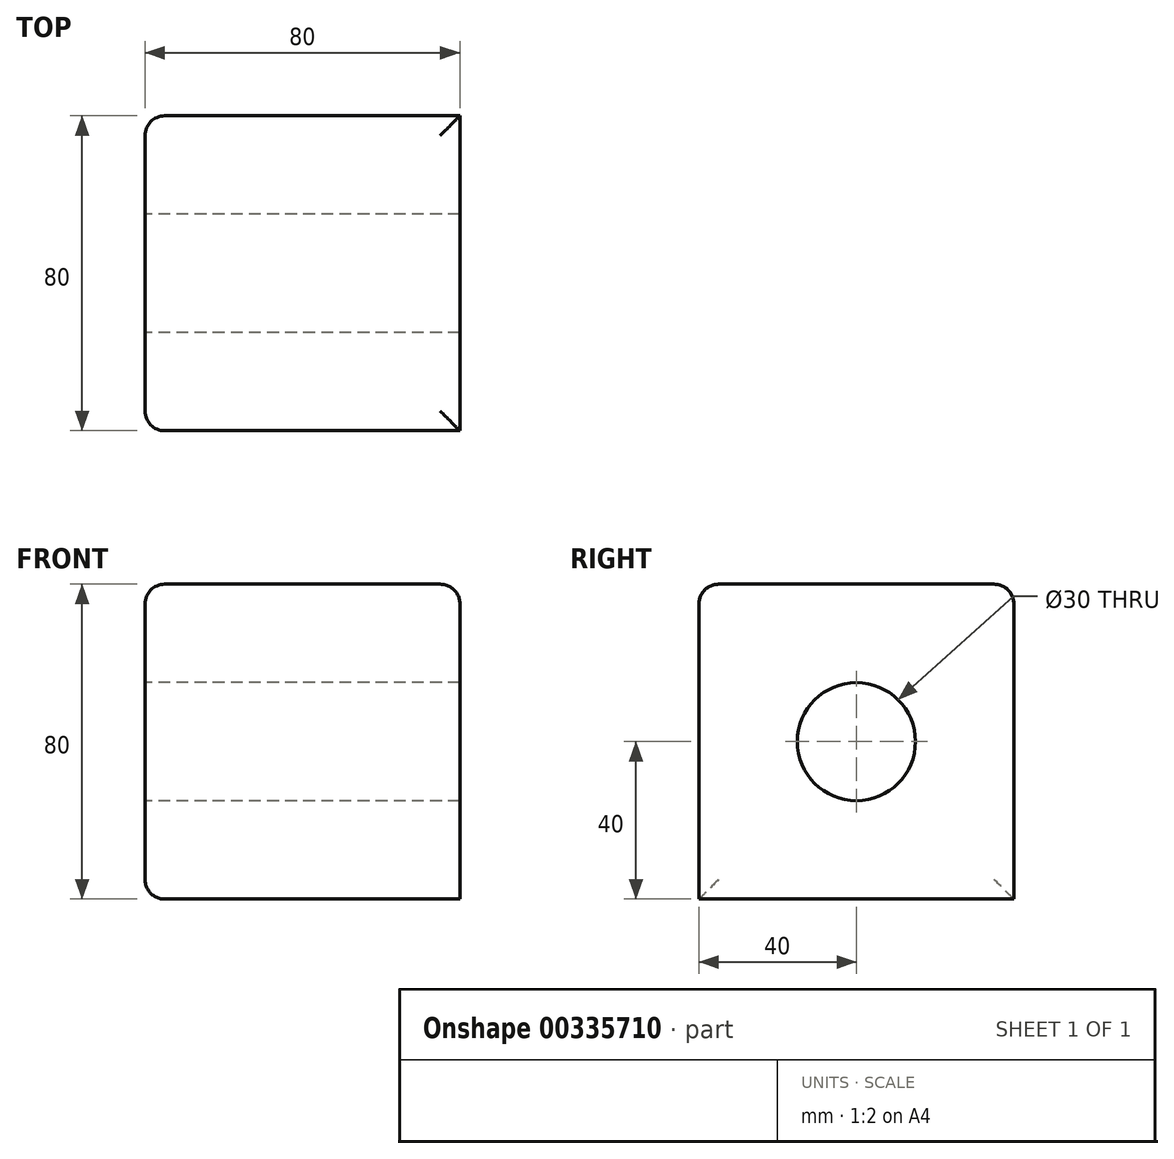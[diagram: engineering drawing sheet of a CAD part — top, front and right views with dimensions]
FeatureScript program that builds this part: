
annotation { "Feature Type Name" : "Feature", "Feature Type Description" : "" }
export const myFeature = defineFeature(function(context is Context, id is Id, definition is map)
    precondition{}
    {
        {
            var Q0;
            Q0=qCreatedBy(makeId("Top.planeOp"),FACE);
            var sketch = newSketch(context, id + "F0", { "sketchPlane" : qUnion([Q0])});
            skLineSegment(sketch, "E0.bottom", {"start": v(40, -40) * mm, "end": v(-40, -40) * mm});
            skLineSegment(sketch, "E0.top", {"start": v(40, 40) * mm, "end": v(-40, 40) * mm});
            skLineSegment(sketch, "E0.left", {"start": v(40, -40) * mm, "end": v(40, 40) * mm});
            skLineSegment(sketch, "E0.right", {"start": v(-40, -40) * mm, "end": v(-40, 40) * mm});
            skPoint(sketch, "E0.middle", {"position": v(0, 0) * mm});
            skSolve(sketch);
        }
        {
            var Q0;
            Q0=makeQuery(id+"F0.imprint","IMPRINT",FACE,{"disambiguationData":[TD([[makeQuery(id+"F0.imprint","IMPRINT",EDGE,{"derivedFrom":sQuery(id+"F0.wireOp",EDGE,"E0.bottom")}),-1.0]])]});
            extrude(context, id + "F1", {"entities" : qUnion([Q0]), "endBound" : BoundingType.SYMMETRIC, "depth" : 80 * mm});
        }
        {
            var Q0;
            Q0=makeQuery(id+"F1.opExtrude","CAP_EDGE",EDGE,{"disambiguationData":[OSD([sQuery(id+"F0.wireOp",EDGE,"E0.right")])],"isStart":false});
            var Q1;
            Q1=makeQuery(id+"F1.opExtrude","CAP_FACE",FACE,{"disambiguationData":[OSD([sQuery(id+"F0.wireOp",EDGE,"E0.bottom"),sQuery(id+"F0.wireOp",EDGE,"E0.top"),sQuery(id+"F0.wireOp",EDGE,"E0.left"),sQuery(id+"F0.wireOp",EDGE,"E0.right")])],"isStart":false});
            var Q2;
            Q2=makeQuery(id+"F1.opExtrude","SWEPT_EDGE",EDGE,{"disambiguationData":[OSD([sQuery(id+"F0.wireOp",EDGE,"E0.top"),sQuery(id+"F0.wireOp",EDGE,"E0.right")])]});
            var Q3;
            Q3=makeQuery(id+"F1.opExtrude","CAP_EDGE",EDGE,{"disambiguationData":[OSD([sQuery(id+"F0.wireOp",EDGE,"E0.right")])],"isStart":true});
            var Q4;
            Q4=makeQuery(id+"F1.opExtrude","SWEPT_FACE",FACE,{"disambiguationData":[OSD([sQuery(id+"F0.wireOp",EDGE,"E0.right")])]});
            fillet(context, id + "F2", {"entities" : qUnion([Q0, Q1, Q2, Q3, Q4]), "radius" : 5 * mm, "tangentPropagation" : true, "allowEdgeOverflow" : false});
        }
        {
            var Q0;
            Q0=makeQuery(id+"F1.opExtrude","SWEPT_FACE",FACE,{"disambiguationData":[OSD([sQuery(id+"F0.wireOp",EDGE,"E0.right")])]});
            var sketch = newSketch(context, id + "F3", { "sketchPlane" : qUnion([Q0])});
            skCircle(sketch, "E1", {"center": v(0, 0) * mm, "radius": 15 * mm});
            skSolve(sketch);
        }
        {
            var Q0;
            Q0=makeQuery(id+"F3.imprint","IMPRINT",FACE,{"disambiguationData":[TD([[makeQuery(id+"F3.imprint","IMPRINT",EDGE,{"derivedFrom":sQuery(id+"F3.wireOp",EDGE,"E1")}),1.0]])]});
            extrude(context, id + "F4", {"entities" : qUnion([Q0]), "operationType" : NewBodyOperationType.REMOVE, "endBound" : BoundingType.THROUGH_ALL, "oppositeDirection" : true, "depth" : 25 * mm});
        }
    });
